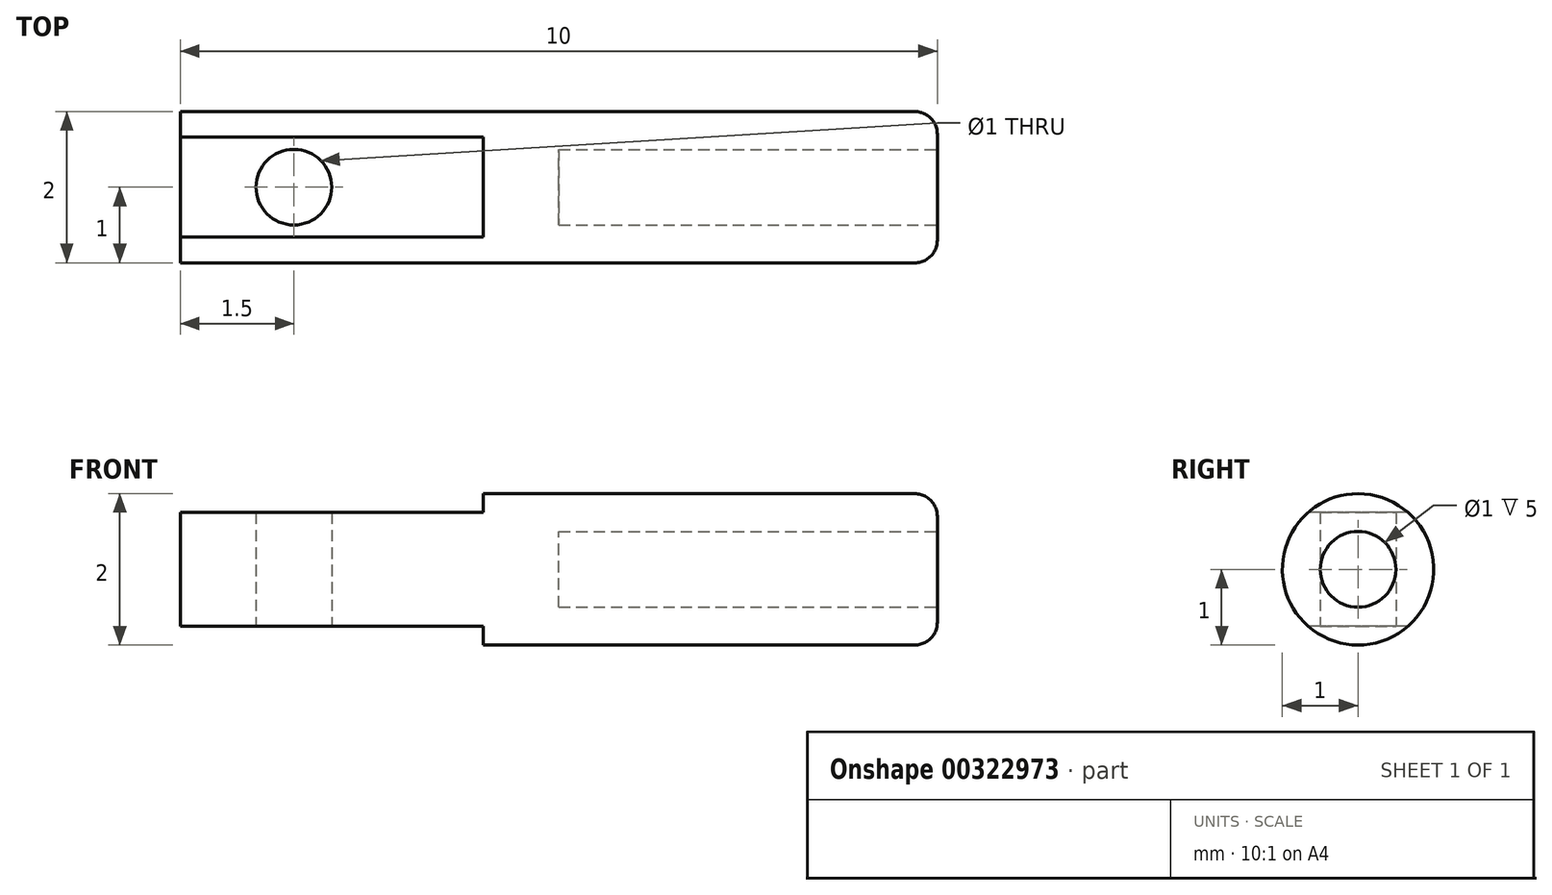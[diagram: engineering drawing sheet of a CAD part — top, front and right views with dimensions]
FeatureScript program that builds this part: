
annotation { "Feature Type Name" : "Feature", "Feature Type Description" : "" }
export const myFeature = defineFeature(function(context is Context, id is Id, definition is map)
    precondition{}
    {
        {
            var Q0;
            Q0=qCreatedBy(makeId("Front.planeOp"),FACE);
            var sketch = newSketch(context, id + "F0", { "sketchPlane" : qUnion([Q0])});
            skLineSegment(sketch, "E0", {"start": v(0, 0) * mm, "end": v(0, 1) * mm});
            skLineSegment(sketch, "E1", {"start": v(0, 1) * mm, "end": v(10, 1) * mm});
            skLineSegment(sketch, "E2", {"start": v(10, 1) * mm, "end": v(10, 0.5) * mm});
            skLineSegment(sketch, "E3", {"start": v(10, 0.5) * mm, "end": v(5, 0.5) * mm});
            skLineSegment(sketch, "E4", {"start": v(5, 0.5) * mm, "end": v(5, 0) * mm});
            skLineSegment(sketch, "E5", {"start": v(5, 0) * mm, "end": v(0, 0) * mm});
            skSolve(sketch);
        }
        {
            var Q0;
            Q0 = qSketchRegion(id + "F0", true);
            var Q1;
            Q1=sQuery(id+"F0.wireOp",EDGE,"E5");
            revolve(context, id + "F1", {"entities" : qUnion([Q0]), "axis" : qUnion([Q1]), "revolveType" : RevolveType.FULL});
        }
        {
            var Q0;
            Q0=qCreatedBy(makeId("Front.planeOp"),FACE);
            var sketch = newSketch(context, id + "F2", { "sketchPlane" : qUnion([Q0])});
            skLineSegment(sketch, "E6", {"start": v(0, 0) * mm, "end": v(0, 0.75) * mm});
            skLineSegment(sketch, "E7", {"start": v(0, 0.75) * mm, "end": v(4, 0.75) * mm});
            skLineSegment(sketch, "E8", {"start": v(4, 0.75) * mm, "end": v(4, 1.08) * mm});
            skLineSegment(sketch, "E9", {"start": v(4, 1.08) * mm, "end": v(0, 1.08) * mm});
            skLineSegment(sketch, "E10", {"start": v(0, 1.08) * mm, "end": v(0, 0.75) * mm});
            skLineSegment(sketch, "E11", {"start": v(0, 0) * mm, "end": v(4.56, 0) * mm, "construction": true});
            skLineSegment(sketch, "E12.MirrorCS", {"start": v(4, -0.75) * mm, "end": v(4, -1.08) * mm});
            skLineSegment(sketch, "E13.MirrorCS", {"start": v(0, -1.08) * mm, "end": v(0, -0.75) * mm});
            skLineSegment(sketch, "E14.MirrorCS", {"start": v(0, -0.75) * mm, "end": v(4, -0.75) * mm});
            skLineSegment(sketch, "E15.MirrorCS", {"start": v(4, -1.08) * mm, "end": v(0, -1.08) * mm});
            skSolve(sketch);
        }
        {
            var Q0;
            Q0 = qSketchRegion(id + "F2", true);
            extrude(context, id + "F3", {"entities" : qUnion([Q0]), "operationType" : NewBodyOperationType.REMOVE, "oppositeDirection" : true, "depth" : 25 * mm, "symmetric" : true});
        }
        {
            var Q0;
            Q0=qCreatedBy(makeId("Top.planeOp"),FACE);
            var sketch = newSketch(context, id + "F4", { "sketchPlane" : qUnion([Q0])});
            skLineSegment(sketch, "E16", {"start": v(0, 0) * mm, "end": v(1.5, 0) * mm, "construction": true});
            skCircle(sketch, "E17", {"center": v(1.5, 0) * mm, "radius": 0.5 * mm});
            skArc(sketch, "E18", {"start": v(0.5, -1.1) * mm, "mid": v(0.18, -0.7) * mm, "end": v(0.02, -0.2) * mm});
            skLineSegment(sketch, "E19", {"start": v(0.5, -1.1) * mm, "end": v(-0.34, -1.1) * mm});
            skLineSegment(sketch, "E20", {"start": v(-0.34, -1.1) * mm, "end": v(-0.34, 0) * mm});
            skArc(sketch, "E21.MirrorCS", {"start": v(0.5, 1.1) * mm, "mid": v(0.18, 0.7) * mm, "end": v(0.02, 0.2) * mm});
            skLineSegment(sketch, "E22.MirrorCS", {"start": v(0.5, 1.1) * mm, "end": v(-0.34, 1.1) * mm});
            skLineSegment(sketch, "E23.MirrorCS", {"start": v(-0.34, 1.1) * mm, "end": v(-0.34, 0) * mm});
            skArc(sketch, "E24", {"start": v(0.02, -0.2) * mm, "mid": v(0, 0) * mm, "end": v(0.02, 0.2) * mm});
            skSolve(sketch);
        }
        {
            var Q0;
            Q0=makeQuery(id+"F4.imprint","IMPRINT",FACE,{"disambiguationData":[TD([[makeQuery(id+"F4.imprint","IMPRINT",EDGE,{"derivedFrom":sQuery(id+"F4.wireOp",EDGE,"E18")}),1.0]])]});
            var Q1;
            Q1=makeQuery(id+"F4.imprint","IMPRINT",FACE,{"disambiguationData":[TD([[makeQuery(id+"F4.imprint","IMPRINT",EDGE,{"derivedFrom":sQuery(id+"F4.wireOp",EDGE,"E17")}),1.0]])]});
            extrude(context, id + "F5", {"entities" : qUnion([Q0, Q1]), "operationType" : NewBodyOperationType.REMOVE, "depth" : 25 * mm, "symmetric" : true});
        }
        {
            var Q0;
            Q0=makeQuery(id+"F1.opRevolve","SWEPT_EDGE",EDGE,{"disambiguationData":[OSD([sQuery(id+"F0.wireOp",EDGE,"E1"),sQuery(id+"F0.wireOp",EDGE,"E2")])]});
            fillet(context, id + "F6", {"entities" : qUnion([Q0]), "radius" : .3 * mm, "tangentPropagation" : true, "allowEdgeOverflow" : false});
        }
    });
